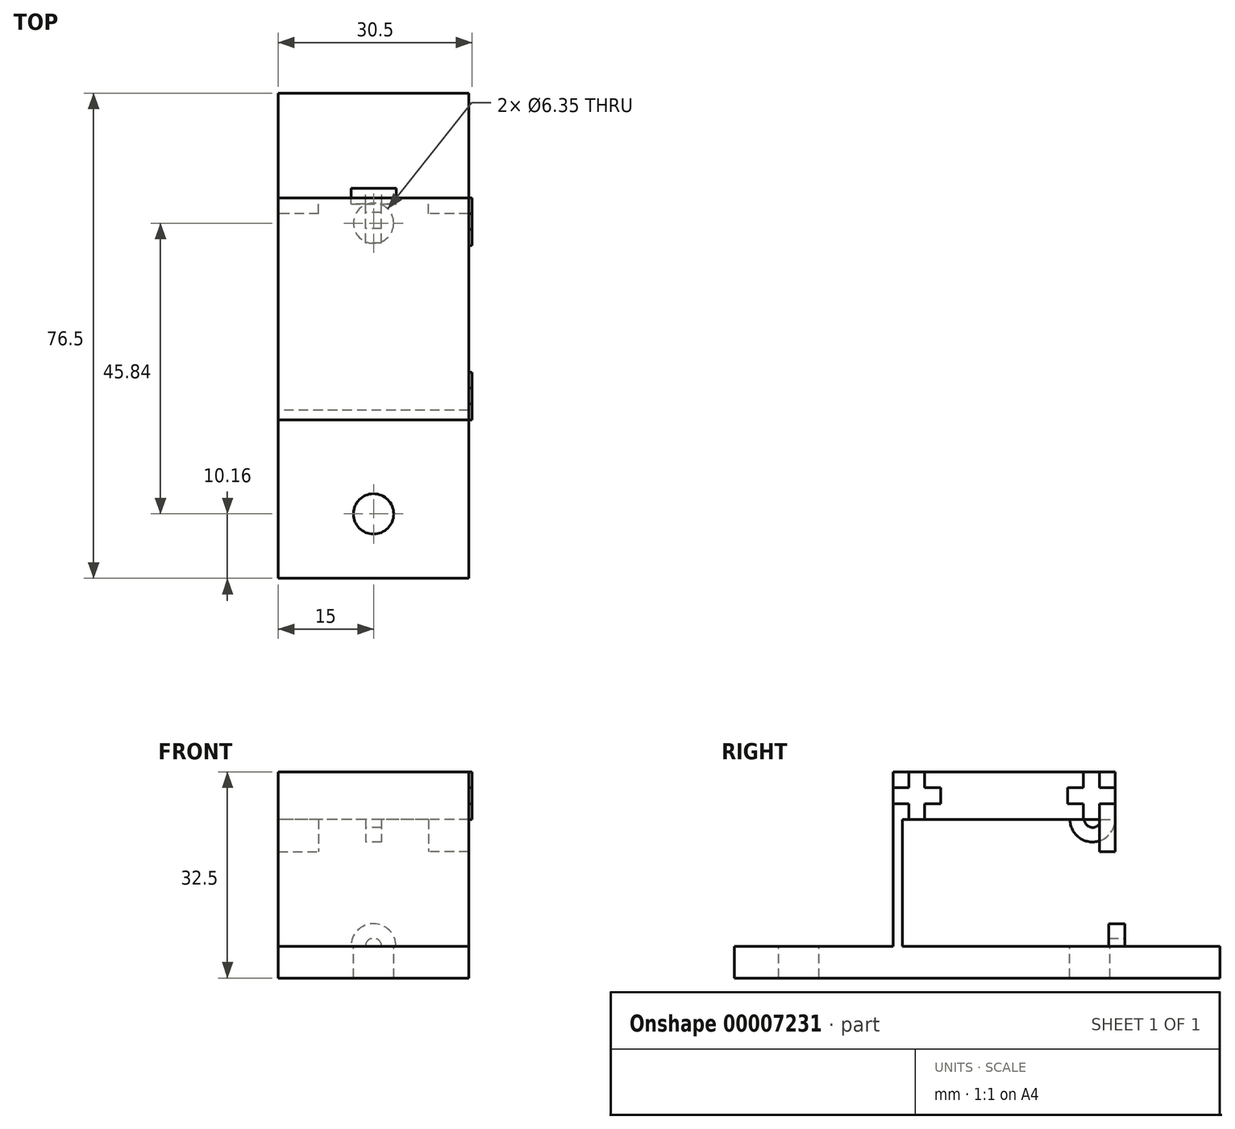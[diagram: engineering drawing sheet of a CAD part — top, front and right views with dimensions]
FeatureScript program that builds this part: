
annotation { "Feature Type Name" : "Feature", "Feature Type Description" : "" }
export const myFeature = defineFeature(function(context is Context, id is Id, definition is map)
    precondition{}
    {
        {
            var Q0;
            Q0=qCreatedBy(makeId("Right.planeOp"),FACE);
            var sketch = newSketch(context, id + "F0", { "sketchPlane" : qUnion([Q0])});
            skLineSegment(sketch, "E0", {"start": v(1.5, 25) * mm, "end": v(32.5, 25) * mm});
            skLineSegment(sketch, "E1", {"start": v(35, 25) * mm, "end": v(35, 32.5) * mm});
            skLineSegment(sketch, "E2", {"start": v(35, 32.5) * mm, "end": v(0, 32.5) * mm});
            skLineSegment(sketch, "E3", {"start": v(0, 32.5) * mm, "end": v(0, 5) * mm});
            skLineSegment(sketch, "E4", {"start": v(0, 0) * mm, "end": v(51.5, 0) * mm});
            skLineSegment(sketch, "E5", {"start": v(1.5, 25) * mm, "end": v(1.5, 5) * mm});
            skLineSegment(sketch, "E6", {"start": v(1.5, 5) * mm, "end": v(51.5, 5) * mm});
            skLineSegment(sketch, "E7", {"start": v(51.5, 5) * mm, "end": v(51.5, 0) * mm});
            skPoint(sketch, "E8", {"position": v(32.5, 25) * mm});
            skPoint(sketch, "E9", {"position": v(0, 25) * mm});
            skPoint(sketch, "E10", {"position": v(0, 5) * mm});
            skLineSegment(sketch, "E11", {"start": v(0, 5) * mm, "end": v(-25, 5) * mm});
            skLineSegment(sketch, "E12", {"start": v(-25, 5) * mm, "end": v(-25, 0) * mm});
            skLineSegment(sketch, "E13", {"start": v(-25, 0) * mm, "end": v(0, 0) * mm});
            skPoint(sketch, "E14.end.orphan", {"position": v(35, 17.46) * mm});
            skLineSegment(sketch, "E15", {"start": v(32.5, 25) * mm, "end": v(35, 25) * mm});
            skSolve(sketch);
        }
        {
            var Q0;
            Q0=qSketchRegion(id+"F0",true);
            extrude(context, id + "F1", {"entities" : qUnion([Q0]), "depth" : 30 * mm});
        }
        {
            var Q0;
            Q0=makeQuery(id+"F1.opExtrude","CAP_FACE",FACE,{"disambiguationData":[OSD([sQuery(id+"F0.wireOp",EDGE,"E0"),sQuery(id+"F0.wireOp",EDGE,"E1"),sQuery(id+"F0.wireOp",EDGE,"E2"),sQuery(id+"F0.wireOp",EDGE,"E3"),sQuery(id+"F0.wireOp",EDGE,"E4"),sQuery(id+"F0.wireOp",EDGE,"E5"),sQuery(id+"F0.wireOp",EDGE,"E6"),sQuery(id+"F0.wireOp",EDGE,"E7"),sQuery(id+"F0.wireOp",EDGE,"E11"),sQuery(id+"F0.wireOp",EDGE,"E12"),sQuery(id+"F0.wireOp",EDGE,"E13"),sQuery(id+"F0.wireOp",EDGE,"E15")])],"isStart":false});
            var sketch = newSketch(context, id + "F2", { "sketchPlane" : qUnion([Q0])});
            skArc(sketch, "E16", {"start": v(27.89, 25) * mm, "mid": v(31.44, 21.44) * mm, "end": v(35, 25) * mm});
            skArc(sketch, "E17", {"start": v(30.17, 25) * mm, "mid": v(31.44, 23.73) * mm, "end": v(32.71, 25) * mm});
            skLineSegment(sketch, "E18", {"start": v(30.17, 25) * mm, "end": v(27.89, 25) * mm});
            skLineSegment(sketch, "E19", {"start": v(27.89, 25) * mm, "end": v(30.17, 25) * mm});
            skLineSegment(sketch, "E20", {"start": v(32.71, 25) * mm, "end": v(35, 25) * mm});
            skSolve(sketch);
        }
        {
            var Q0;
            Q0=qSketchRegion(id+"F2",true);
            extrude(context, id + "F3", {"entities" : qUnion([Q0]), "depth" : 2.5 * mm});
        }
        {
            var Q0;
            Q0=makeQuery(id+"F3.opExtrude","SWEPT_BODY",BODY,{"disambiguationData":[OSD([sQuery(id+"F2.wireOp",EDGE,"E16"),sQuery(id+"F2.wireOp",EDGE,"E17"),sQuery(id+"F2.wireOp",EDGE,"E19"),sQuery(id+"F2.wireOp",EDGE,"E20")])]});
            var Q1;
            Q1=makeQuery(id+"F1.opExtrude","SWEPT_EDGE",EDGE,{"disambiguationData":[OSD([sQuery(id+"F0.wireOp",EDGE,"E1"),sQuery(id+"F0.wireOp",EDGE,"E15")])]});
            transform(context, id + "F4", {"entities" : qUnion([Q0]), "transformType" : TransformType.TRANSLATION_DISTANCE, "transformDirection" : qUnion([Q1]), "distance" : 16.25 * mm, "makeCopy" : false});
        }
        {
            var Q0;
            Q0=makeQuery(id+"F1.opExtrude","SWEPT_FACE",FACE,{"disambiguationData":[OSD([sQuery(id+"F0.wireOp",EDGE,"E7")])]});
            var sketch = newSketch(context, id + "F5", { "sketchPlane" : qUnion([Q0])});
            skArc(sketch, "E21", {"start": v(-11.44, 5) * mm, "mid": v(-15, 8.56) * mm, "end": v(-18.56, 5) * mm});
            skArc(sketch, "E22", {"start": v(-13.73, 5) * mm, "mid": v(-15, 6.27) * mm, "end": v(-16.27, 5) * mm});
            skLineSegment(sketch, "E23", {"start": v(-18.56, 5) * mm, "end": v(-16.27, 5) * mm});
            skLineSegment(sketch, "E24", {"start": v(-13.73, 5) * mm, "end": v(-11.44, 5) * mm});
            skSolve(sketch);
        }
        {
            var Q0;
            Q0=qSketchRegion(id+"F5",true);
            extrude(context, id + "F6", {"entities" : qUnion([Q0]), "oppositeDirection" : true, "depth" : 2.5 * mm});
        }
        {
            var Q0;
            Q0=makeQuery(id+"F6.opExtrude","SWEPT_BODY",BODY,{"disambiguationData":[OSD([sQuery(id+"F5.wireOp",EDGE,"E21"),sQuery(id+"F5.wireOp",EDGE,"E22"),sQuery(id+"F5.wireOp",EDGE,"E23"),sQuery(id+"F5.wireOp",EDGE,"E24")])]});
            var Q1;
            Q1=makeQuery(id+"F1.opExtrude","CAP_EDGE",EDGE,{"disambiguationData":[OSD([sQuery(id+"F0.wireOp",EDGE,"E6")])],"isStart":false});
            transform(context, id + "F7", {"entities" : qUnion([Q0]), "transformType" : TransformType.TRANSLATION_DISTANCE, "transformDirection" : qUnion([Q1]), "distance" : 15 * mm, "oppositeDirection" : true, "makeCopy" : false});
        }
        {
            var Q0;
            Q0=makeQuery(id+"F1.opExtrude","SWEPT_FACE",FACE,{"disambiguationData":[OSD([sQuery(id+"F0.wireOp",EDGE,"E1")])]});
            var sketch = newSketch(context, id + "F8", { "sketchPlane" : qUnion([Q0])});
            skLineSegment(sketch, "E25.bottom", {"start": v(-30, 25) * mm, "end": v(-23.65, 25) * mm});
            skLineSegment(sketch, "E25.top", {"start": v(-30, 19.92) * mm, "end": v(-23.65, 19.92) * mm});
            skLineSegment(sketch, "E25.left", {"start": v(-30, 25) * mm, "end": v(-30, 19.92) * mm});
            skLineSegment(sketch, "E25.right", {"start": v(-23.65, 25) * mm, "end": v(-23.65, 19.92) * mm});
            skLineSegment(sketch, "E26.bottom", {"start": v(0, 25) * mm, "end": v(-6.35, 25) * mm});
            skLineSegment(sketch, "E26.top", {"start": v(0, 19.92) * mm, "end": v(-6.35, 19.92) * mm});
            skLineSegment(sketch, "E26.left", {"start": v(0, 25) * mm, "end": v(0, 19.92) * mm});
            skLineSegment(sketch, "E26.right", {"start": v(-6.35, 25) * mm, "end": v(-6.35, 19.92) * mm});
            skLineSegment(sketch, "E27", {"start": v(-15, 25) * mm, "end": v(-15, 12.44) * mm, "construction": true});
            skSolve(sketch);
        }
        {
            var Q0;
            Q0=qSketchRegion(id+"F8",true);
            extrude(context, id + "F9", {"entities" : qUnion([Q0]), "oppositeDirection" : true, "depth" : 2.5 * mm});
        }
        {
            var Q0;
            Q0=makeQuery(id+"F1.opExtrude","SWEPT_BODY",BODY,{"disambiguationData":[OSD([sQuery(id+"F0.wireOp",EDGE,"E0"),sQuery(id+"F0.wireOp",EDGE,"E1"),sQuery(id+"F0.wireOp",EDGE,"E2"),sQuery(id+"F0.wireOp",EDGE,"E3"),sQuery(id+"F0.wireOp",EDGE,"E4"),sQuery(id+"F0.wireOp",EDGE,"E5"),sQuery(id+"F0.wireOp",EDGE,"E6"),sQuery(id+"F0.wireOp",EDGE,"E7"),sQuery(id+"F0.wireOp",EDGE,"E11"),sQuery(id+"F0.wireOp",EDGE,"E12"),sQuery(id+"F0.wireOp",EDGE,"E13"),sQuery(id+"F0.wireOp",EDGE,"E15")])]});
            var Q1;
            Q1=makeQuery(id+"F3.opExtrude","SWEPT_BODY",BODY,{"disambiguationData":[OSD([sQuery(id+"F2.wireOp",EDGE,"E16"),sQuery(id+"F2.wireOp",EDGE,"E17"),sQuery(id+"F2.wireOp",EDGE,"E19"),sQuery(id+"F2.wireOp",EDGE,"E20")])]});
            var Q2;
            Q2=makeQuery(id+"F9.opExtrude","SWEPT_BODY",BODY,{"disambiguationData":[OSD([sQuery(id+"F8.wireOp",EDGE,"E26.bottom"),sQuery(id+"F8.wireOp",EDGE,"E26.top"),sQuery(id+"F8.wireOp",EDGE,"E26.left"),sQuery(id+"F8.wireOp",EDGE,"E26.right")])]});
            var Q3;
            Q3=makeQuery(id+"F9.opExtrude","SWEPT_BODY",BODY,{"disambiguationData":[OSD([sQuery(id+"F8.wireOp",EDGE,"E25.bottom"),sQuery(id+"F8.wireOp",EDGE,"E25.top"),sQuery(id+"F8.wireOp",EDGE,"E25.left"),sQuery(id+"F8.wireOp",EDGE,"E25.right")])]});
            var Q4;
            Q4=makeQuery(id+"F6.opExtrude","SWEPT_BODY",BODY,{"disambiguationData":[OSD([sQuery(id+"F5.wireOp",EDGE,"E21"),sQuery(id+"F5.wireOp",EDGE,"E22"),sQuery(id+"F5.wireOp",EDGE,"E23"),sQuery(id+"F5.wireOp",EDGE,"E24")])]});
            booleanBodies(context, id + "F10", {"operationType" : BooleanOperationType.UNION, "tools" : qUnion([Q0, Q1, Q2, Q3, Q4])});
        }
        {
            var Q0;
            Q0=makeQuery(id+"F10.opBoolean","MERGE",FACE,{"derivedFrom":[makeQuery(id+"F1.opExtrude","CAP_FACE",FACE,{"disambiguationData":[OSD([sQuery(id+"F0.wireOp",EDGE,"E0"),sQuery(id+"F0.wireOp",EDGE,"E1"),sQuery(id+"F0.wireOp",EDGE,"E2"),sQuery(id+"F0.wireOp",EDGE,"E3"),sQuery(id+"F0.wireOp",EDGE,"E4"),sQuery(id+"F0.wireOp",EDGE,"E5"),sQuery(id+"F0.wireOp",EDGE,"E6"),sQuery(id+"F0.wireOp",EDGE,"E7"),sQuery(id+"F0.wireOp",EDGE,"E11"),sQuery(id+"F0.wireOp",EDGE,"E12"),sQuery(id+"F0.wireOp",EDGE,"E13"),sQuery(id+"F0.wireOp",EDGE,"E15")])],"isStart":false}),makeQuery(id+"F9.opExtrude","SWEPT_FACE",FACE,{"disambiguationData":[OSD([sQuery(id+"F8.wireOp",EDGE,"E25.left")])]})]});
            var sketch = newSketch(context, id + "F11", { "sketchPlane" : qUnion([Q0])});
            skLineSegment(sketch, "E28", {"start": v(17.5, 32.5) * mm, "end": v(17.5, 25) * mm, "construction": true});
            skLineSegment(sketch, "E29.bottom", {"start": v(0, 30) * mm, "end": v(2.5, 30) * mm});
            skLineSegment(sketch, "E29.top", {"start": v(0, 27.5) * mm, "end": v(2.5, 27.5) * mm});
            skLineSegment(sketch, "E29.left", {"start": v(0, 30) * mm, "end": v(0, 27.5) * mm});
            skLineSegment(sketch, "E29.right", {"start": v(7.5, 30) * mm, "end": v(7.5, 27.5) * mm});
            skLineSegment(sketch, "E30.bottom", {"start": v(27.5, 30) * mm, "end": v(30, 30) * mm});
            skLineSegment(sketch, "E30.top", {"start": v(27.5, 27.5) * mm, "end": v(30, 27.5) * mm});
            skLineSegment(sketch, "E30.left", {"start": v(27.5, 30) * mm, "end": v(27.5, 27.5) * mm});
            skLineSegment(sketch, "E30.right", {"start": v(35, 30) * mm, "end": v(35, 27.5) * mm});
            skLineSegment(sketch, "E31.bottom", {"start": v(2.5, 32.5) * mm, "end": v(5, 32.5) * mm});
            skLineSegment(sketch, "E31.top", {"start": v(2.5, 25) * mm, "end": v(5, 25) * mm});
            skLineSegment(sketch, "E31.left", {"start": v(2.5, 32.5) * mm, "end": v(2.5, 30) * mm});
            skLineSegment(sketch, "E31.right", {"start": v(5, 32.5) * mm, "end": v(5, 30) * mm});
            skLineSegment(sketch, "E32.bottom", {"start": v(30, 32.5) * mm, "end": v(32.5, 32.5) * mm});
            skLineSegment(sketch, "E32.top", {"start": v(30, 25) * mm, "end": v(32.5, 25) * mm});
            skLineSegment(sketch, "E32.left", {"start": v(30, 32.5) * mm, "end": v(30, 30) * mm});
            skLineSegment(sketch, "E32.right", {"start": v(32.5, 32.5) * mm, "end": v(32.5, 30) * mm});
            skPoint(sketch, "E33", {"position": v(2.5, 30) * mm});
            skPoint(sketch, "E34", {"position": v(5, 30) * mm});
            skPoint(sketch, "E35", {"position": v(5, 27.5) * mm});
            skPoint(sketch, "E36", {"position": v(2.5, 27.5) * mm});
            skPoint(sketch, "E37", {"position": v(30, 30) * mm});
            skPoint(sketch, "E38", {"position": v(32.5, 30) * mm});
            skPoint(sketch, "E39", {"position": v(32.5, 27.5) * mm});
            skPoint(sketch, "E40", {"position": v(30, 27.5) * mm});
            skLineSegment(sketch, "E41.trimOffspring", {"start": v(5, 27.5) * mm, "end": v(5, 25) * mm});
            skLineSegment(sketch, "E42.trimOffspring", {"start": v(5, 30) * mm, "end": v(7.5, 30) * mm});
            skLineSegment(sketch, "E43.trimOffspring", {"start": v(2.5, 27.5) * mm, "end": v(2.5, 25) * mm});
            skLineSegment(sketch, "E44.trimOffspring", {"start": v(5, 27.5) * mm, "end": v(7.5, 27.5) * mm});
            skLineSegment(sketch, "E45.trimOffspring", {"start": v(32.5, 30) * mm, "end": v(35, 30) * mm});
            skLineSegment(sketch, "E46.trimOffspring", {"start": v(30, 27.5) * mm, "end": v(30, 25) * mm});
            skLineSegment(sketch, "E47.trimOffspring", {"start": v(32.5, 27.5) * mm, "end": v(35, 27.5) * mm});
            skLineSegment(sketch, "E48.trimOffspring", {"start": v(32.5, 27.5) * mm, "end": v(32.5, 25) * mm});
            skSolve(sketch);
        }
        {
            var Q0;
            Q0=qSketchRegion(id+"F11",true);
            extrude(context, id + "F12", {"entities" : qUnion([Q0]), "depth" : 0.5 * mm});
        }
        {
            var Q0;
            Q0=makeQuery(id+"F1.opExtrude","SWEPT_FACE",FACE,{"disambiguationData":[OSD([sQuery(id+"F0.wireOp",EDGE,"E6")])]});
            var sketch = newSketch(context, id + "F13", { "sketchPlane" : qUnion([Q0])});
            skLineSegment(sketch, "E49", {"start": v(15, 51.5) * mm, "end": v(15, -25) * mm, "construction": true});
            skCircle(sketch, "E50", {"center": v(15, 31) * mm, "radius": 3.18 * mm});
            skCircle(sketch, "E51", {"center": v(15, -14.84) * mm, "radius": 3.18 * mm});
            skSolve(sketch);
        }
        {
            var Q0;
            Q0=qSketchRegion(id+"F13",true);
            extrude(context, id + "F14", {"entities" : qUnion([Q0]), "operationType" : NewBodyOperationType.REMOVE, "oppositeDirection" : true, "depth" : 5 * mm});
        }
    });
